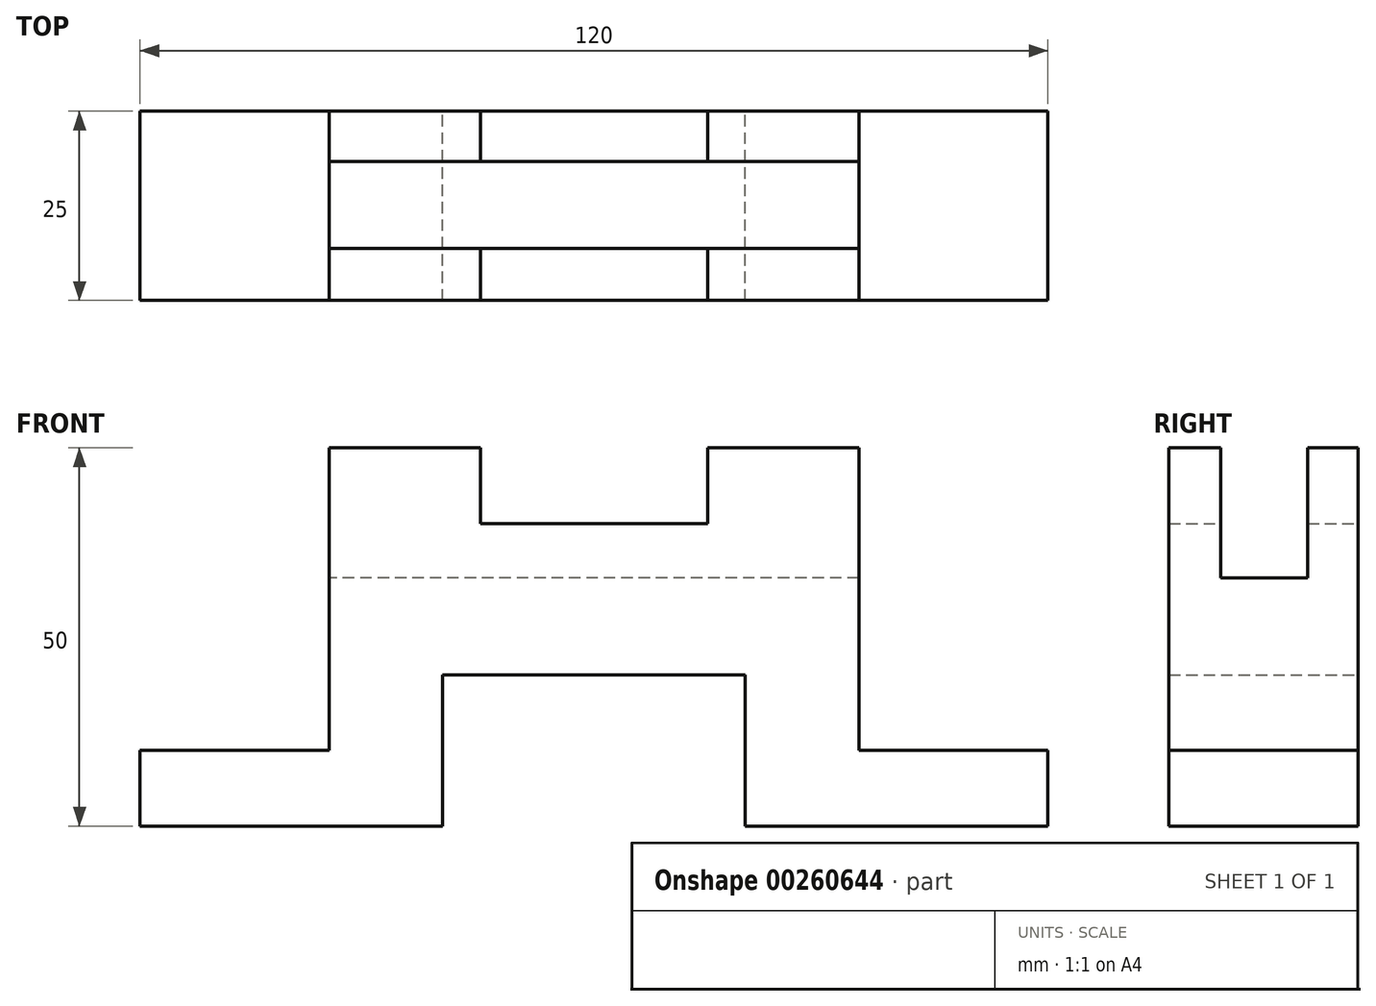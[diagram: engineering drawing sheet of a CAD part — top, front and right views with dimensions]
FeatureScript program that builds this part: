
annotation { "Feature Type Name" : "Feature", "Feature Type Description" : "" }
export const myFeature = defineFeature(function(context is Context, id is Id, definition is map)
    precondition{}
    {
        {
            var Q0;
            Q0=qCreatedBy(makeId("Front.planeOp"),FACE);
            var sketch = newSketch(context, id + "F0", { "sketchPlane" : qUnion([Q0])});
            skLineSegment(sketch, "E0", {"start": v(-60, 0) * mm, "end": v(-20, 0) * mm});
            skLineSegment(sketch, "E1", {"start": v(-20, 0) * mm, "end": v(-20, 20) * mm});
            skLineSegment(sketch, "E2", {"start": v(-20, 20) * mm, "end": v(20, 20) * mm});
            skLineSegment(sketch, "E3", {"start": v(20, 20) * mm, "end": v(20, 0) * mm});
            skLineSegment(sketch, "E4", {"start": v(20, 0) * mm, "end": v(60, 0) * mm});
            skLineSegment(sketch, "E5", {"start": v(35, 50) * mm, "end": v(15, 50) * mm});
            skLineSegment(sketch, "E6", {"start": v(15, 50) * mm, "end": v(15, 40) * mm});
            skLineSegment(sketch, "E7", {"start": v(15, 40) * mm, "end": v(-15, 40) * mm});
            skLineSegment(sketch, "E8", {"start": v(-15, 40) * mm, "end": v(-15, 50) * mm});
            skLineSegment(sketch, "E9", {"start": v(-15, 50) * mm, "end": v(-35, 50) * mm});
            skLineSegment(sketch, "E10", {"start": v(-35, 50) * mm, "end": v(-35, 10) * mm});
            skLineSegment(sketch, "E11", {"start": v(-35, 10) * mm, "end": v(-60, 10) * mm});
            skLineSegment(sketch, "E12", {"start": v(-60, 10) * mm, "end": v(-60, 0) * mm});
            skLineSegment(sketch, "E13", {"start": v(35, 50) * mm, "end": v(35, 10) * mm});
            skLineSegment(sketch, "E14", {"start": v(35, 10) * mm, "end": v(60, 10) * mm});
            skLineSegment(sketch, "E15", {"start": v(60, 10) * mm, "end": v(60, 0) * mm});
            skPoint(sketch, "E16", {"position": v(0, 20) * mm});
            skSolve(sketch);
        }
        {
            var Q0;
            Q0 = qSketchRegion(id + "F0", true);
            extrude(context, id + "F1", {"entities" : qUnion([Q0]), "depth" : 25 * mm});
        }
        {
            var Q0;
            Q0=makeQuery(id+"F1.opExtrude","SWEPT_FACE",FACE,{"disambiguationData":[OSD([sQuery(id+"F0.wireOp",EDGE,"E10")])]});
            var sketch = newSketch(context, id + "F2", { "sketchPlane" : qUnion([Q0])});
            skLineSegment(sketch, "E17.bottom", {"start": v(-57.4, -31.36) * mm, "end": v(-50.81, -31.36) * mm});
            skLineSegment(sketch, "E18.bottom", {"start": v(18.14, 50) * mm, "end": v(6.66, 50) * mm});
            skLineSegment(sketch, "E18.top", {"start": v(18.14, 32.8) * mm, "end": v(6.66, 32.8) * mm});
            skLineSegment(sketch, "E18.left", {"start": v(18.14, 50) * mm, "end": v(18.14, 32.8) * mm});
            skLineSegment(sketch, "E18.right", {"start": v(6.66, 50) * mm, "end": v(6.66, 32.8) * mm});
            skSolve(sketch);
        }
        {
            var Q0;
            Q0 = qSketchRegion(id + "F2", true);
            extrude(context, id + "F3", {"entities" : qUnion([Q0]), "operationType" : NewBodyOperationType.REMOVE, "oppositeDirection" : true, "depth" : 76.6 * mm});
        }
    });
